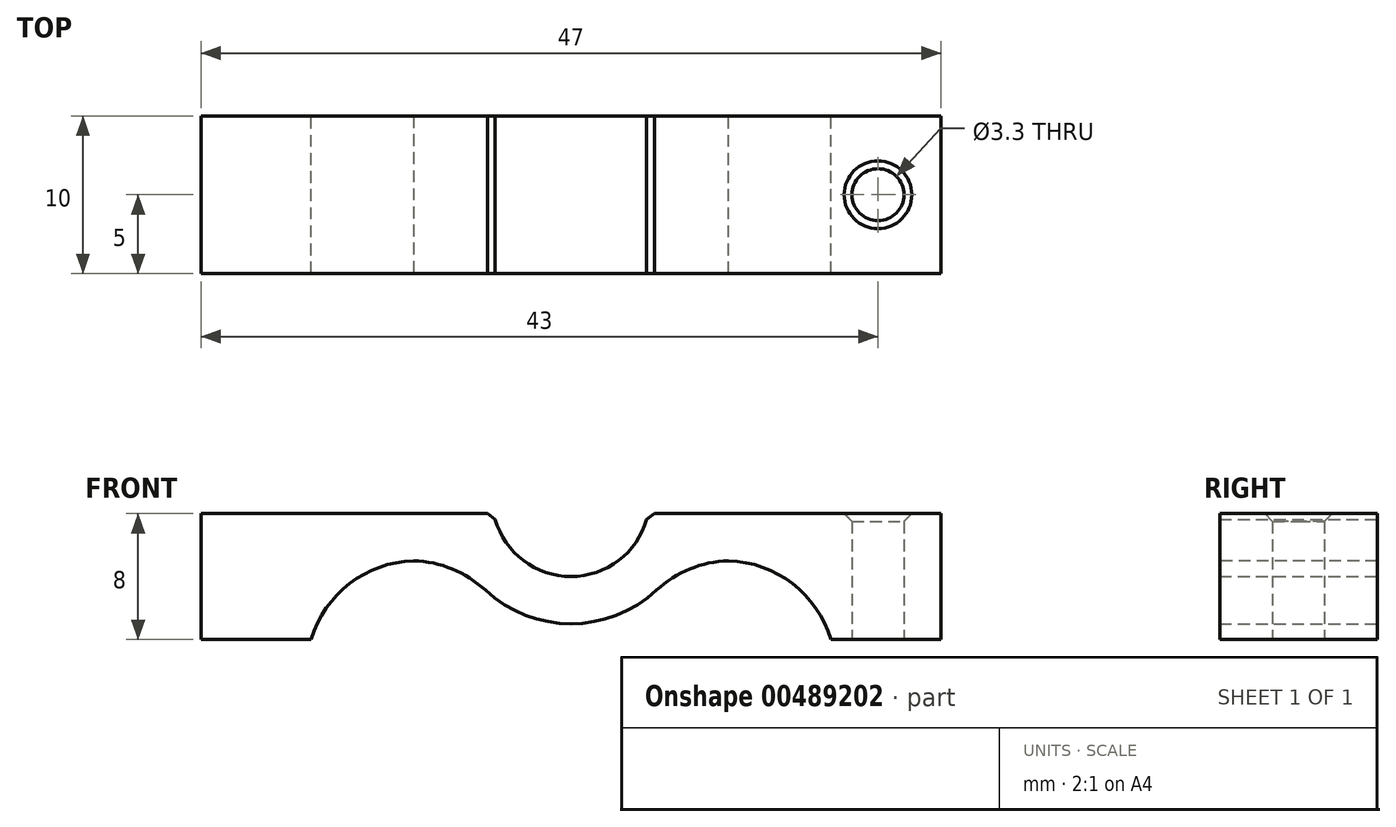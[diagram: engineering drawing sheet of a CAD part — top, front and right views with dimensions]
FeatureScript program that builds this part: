
annotation { "Feature Type Name" : "Feature", "Feature Type Description" : "" }
export const myFeature = defineFeature(function(context is Context, id is Id, definition is map)
    precondition{}
    {
        {
            var Q0;
            Q0=qCreatedBy(makeId("Front.planeOp"),FACE);
            var sketch = newSketch(context, id + "F0", { "sketchPlane" : qUnion([Q0])});
            skLineSegment(sketch, "E0", {"start": v(0, 20.98) * mm, "end": v(0, 0) * mm, "construction": true});
            skLineSegment(sketch, "E1", {"start": v(23.5, -1) * mm, "end": v(23.5, -9) * mm});
            skLineSegment(sketch, "E2", {"start": v(23.5, -9) * mm, "end": v(16.5, -9) * mm});
            skArc(sketch, "E3", {"start": v(0, -5) * mm, "mid": v(3.16, -3.87) * mm, "end": v(4.9, -1) * mm});
            skLineSegment(sketch, "E4", {"start": v(23.5, -1) * mm, "end": v(4.9, -1) * mm});
            skLineSegment(sketch, "E5.MirrorCS", {"start": v(-23.5, -1) * mm, "end": v(-23.5, -9) * mm});
            skLineSegment(sketch, "E6.MirrorCS", {"start": v(-23.5, -9) * mm, "end": v(-16.5, -9) * mm});
            skArc(sketch, "E7.MirrorCS", {"start": v(0, -5) * mm, "mid": v(-3.16, -3.87) * mm, "end": v(-4.9, -1) * mm});
            skLineSegment(sketch, "E8.MirrorCS", {"start": v(-23.5, -1) * mm, "end": v(-4.9, -1) * mm});
            skLineSegment(sketch, "E9", {"start": v(16.5, -4) * mm, "end": v(16.5, -9) * mm});
            skLineSegment(sketch, "E10.MirrorCS", {"start": v(-16.5, -4) * mm, "end": v(-16.5, -9) * mm});
            skArc(sketch, "E11.0", {"start": v(0, -8) * mm, "mid": v(4, -6.93) * mm, "end": v(6.93, -4) * mm});
            skLineSegment(sketch, "E11.1", {"start": v(16.5, -4) * mm, "end": v(6.93, -4) * mm});
            skArc(sketch, "E12.MirrorCS", {"start": v(0, -8) * mm, "mid": v(-4, -6.93) * mm, "end": v(-6.93, -4) * mm});
            skLineSegment(sketch, "E13.MirrorCS", {"start": v(-16.5, -4) * mm, "end": v(-6.93, -4) * mm});
            skSolve(sketch);
        }
        {
            var Q0;
            Q0 = qSketchRegion(id + "F0", true);
            extrude(context, id + "F1", {"entities" : qUnion([Q0]), "endBound" : BoundingType.SYMMETRIC, "depth" : 10 * mm});
        }
        {
            var Q0;
            Q0=makeQuery(id+"F1.opExtrude","SWEPT_FACE",FACE,{"disambiguationData":[OSD([sQuery(id+"F0.wireOp",EDGE,"E2")])]});
            var sketch = newSketch(context, id + "F2", { "sketchPlane" : qUnion([Q0])});
            skCircle(sketch, "E14", {"center": v(19.5, 0) * mm, "radius": 1.65 * mm});
            skPoint(sketch, "E14.centerSnap0", {"position": v(23.5, 0) * mm});
            skLineSegment(sketch, "E15", {"start": v(0, -5) * mm, "end": v(0, 5) * mm, "construction": true});
            skSolve(sketch);
        }
        {
            var Q0;
            Q0=makeQuery(id+"F1.opExtrude","SWEPT_EDGE",EDGE,{"disambiguationData":[OSD([sQuery(id+"F0.wireOp",EDGE,"E9"),sQuery(id+"F0.wireOp",EDGE,"E11.1")])]});
            var Q1;
            Q1=makeQuery(id+"F1.opExtrude","SWEPT_EDGE",EDGE,{"disambiguationData":[OSD([sQuery(id+"F0.wireOp",EDGE,"E11.0"),sQuery(id+"F0.wireOp",EDGE,"E11.1")])]});
            var Q2;
            Q2=makeQuery(id+"F1.opExtrude","SWEPT_EDGE",EDGE,{"disambiguationData":[OSD([sQuery(id+"F0.wireOp",EDGE,"E10.MirrorCS"),sQuery(id+"F0.wireOp",EDGE,"E13.MirrorCS")])]});
            var Q3;
            Q3=makeQuery(id+"F1.opExtrude","SWEPT_EDGE",EDGE,{"disambiguationData":[OSD([sQuery(id+"F0.wireOp",EDGE,"E12.MirrorCS"),sQuery(id+"F0.wireOp",EDGE,"E13.MirrorCS")])]});
            fillet(context, id + "F3", {"entities" : qUnion([Q0, Q1, Q2, Q3]), "radius" : 7 * mm, "tangentPropagation" : true, "allowEdgeOverflow" : false});
        }
        {
            var Q0;
            Q0=makeQuery(id+"F1.opExtrude","SWEPT_EDGE",EDGE,{"disambiguationData":[OSD([sQuery(id+"F0.wireOp",EDGE,"E7.MirrorCS"),sQuery(id+"F0.wireOp",EDGE,"E8.MirrorCS")])]});
            var Q1;
            Q1=makeQuery(id+"F1.opExtrude","SWEPT_EDGE",EDGE,{"disambiguationData":[OSD([sQuery(id+"F0.wireOp",EDGE,"E3"),sQuery(id+"F0.wireOp",EDGE,"E4")])]});
            chamfer(context, id + "F4", {"entities" : qUnion([Q0, Q1]), "width" : 0.5 * mm, "tangentPropagation" : true});
        }
        {
            var Q0;
            Q0 = qSketchRegion(id + "F2", true);
            extrude(context, id + "F5", {"entities" : qUnion([Q0]), "operationType" : NewBodyOperationType.REMOVE, "endBound" : BoundingType.THROUGH_ALL, "oppositeDirection" : true, "depth" : 25 * mm});
        }
        {
            var Q0;
            Q0=makeQuery(id+"F5.boolean.opBoolean","COPY",EDGE,{"derivedFrom":makeQuery(id+"F5.opExtrude","CAP_EDGE",EDGE,{"disambiguationData":[OSD([sQuery(id+"F2.wireOp",EDGE,"E14")])],"isStart":true})});
            var Q1;
            Q1=makeQuery(id+"Fq1kqo75WeWk5Tt_1.1.F5.boolean.opBoolean","COPY",EDGE,{"derivedFrom":makeQuery(id+"Fq1kqo75WeWk5Tt_1.1.F5.opExtrude","CAP_EDGE",EDGE,{"disambiguationData":[OSD([sQuery(id+"F2.wireOp",EDGE,"E14")])],"isStart":true})});
            var Q2;
            Q2=makeQuery(id+"F5.boolean.opBoolean","INTERSECT",EDGE,{"derivedFrom":[makeQuery(id+"F1.opExtrude","SWEPT_FACE",FACE,{"disambiguationData":[OSD([sQuery(id+"F0.wireOp",EDGE,"E4")])]}),makeQuery(id+"F5.opExtrude","SWEPT_FACE",FACE,{"disambiguationData":[OSD([sQuery(id+"F2.wireOp",EDGE,"E14")])]})]});
            var Q3;
            Q3=makeQuery(id+"Fq1kqo75WeWk5Tt_1.1.F5.boolean.opBoolean","INTERSECT",EDGE,{"derivedFrom":[makeQuery(id+"F1.opExtrude","SWEPT_FACE",FACE,{"disambiguationData":[OSD([sQuery(id+"F0.wireOp",EDGE,"E8.MirrorCS")])]}),makeQuery(id+"Fq1kqo75WeWk5Tt_1.1.F5.opExtrude","SWEPT_FACE",FACE,{"disambiguationData":[OSD([sQuery(id+"F2.wireOp",EDGE,"E14")])]})]});
            chamfer(context, id + "F6", {"entities" : qUnion([Q0, Q1, Q2, Q3]), "width" : 0.5 * mm, "tangentPropagation" : true});
        }
    });
